# Revit family: Shower-Shower_Door-KOHLER-Levity-K-706010
name_source: partatom
category: Specialty Equipment
units: mm (PartAtom-declared; Revit-internal decimal feet)

## family parameters
Cut with Voids When Loaded = No
Host = Face
OmniClass Number = 23.31.17.17
OmniClass Title = Shower Enclosures
Part Type = Normal
Room Calculation Point = No
Round Connector Dimension = Use Diameter
Shared = No

## types (6) — shared parameters
ADA Compliant = No
Assembly Code = C1030200
Date Modified = 09/06/2022
Default Elevation = 4"
Description = Sliding Shower Door, 74 Inch H x 43-5/8  - 47-5/8 Inch W, With 1/4 Inch Thick Crystal Clear Glass And Blade Handles
Height = 73 9/16"
Length = 3 1/2"
Manufacturer = Kohler Co.
Master Format 2014 = 10 28 19.16
Master Format 2014 Name = Shower Doors
Material = Premium Metal Construction
Product Documentation Link = https://www.us.kohler.com
Product Name = Levity
Product Page URL = https://www.us.kohler.com
URL = https://www.us.kohler.com
WaterSense Certified = No

## per-type parameters (varying)
| type | Finish | Model | Type |
| ABV-Anodized Brushed Bronze | Kohler-Metal-ABV-Anodized_Brushed_Bronze | K-706010-L-ABV | 2 |
| ABZ-Anodized Dark Bronze | Kohler-Metal-ABZ-Anodized_Dark_Bronze | K-706010-L-ABZ | 3 |
| 2MB-Vibrant Brushed Moderne Brass | Kohler-Metal-2MB-Vibrant_Brushed_Moderne_Brass | K-706010-L-2MB | 1 |
| BL-Matte Black | Kohler-Metal-BL-Matte_Black | K-706010-L-BL | 4 |
| NX-Brushed Nickel | Kohler-Metal-NX-Brushed_Nickel | K-706010-L-NX | 5 |
| SHP-Bright Polished Silver | Kohler-Metal-SHP-Bright_Polished_Silver | K-706010-L-SHP | 6 |

## geometry (parser evidence)
native form markers: Sweep x5
no freeform markers — native parametric forms only
